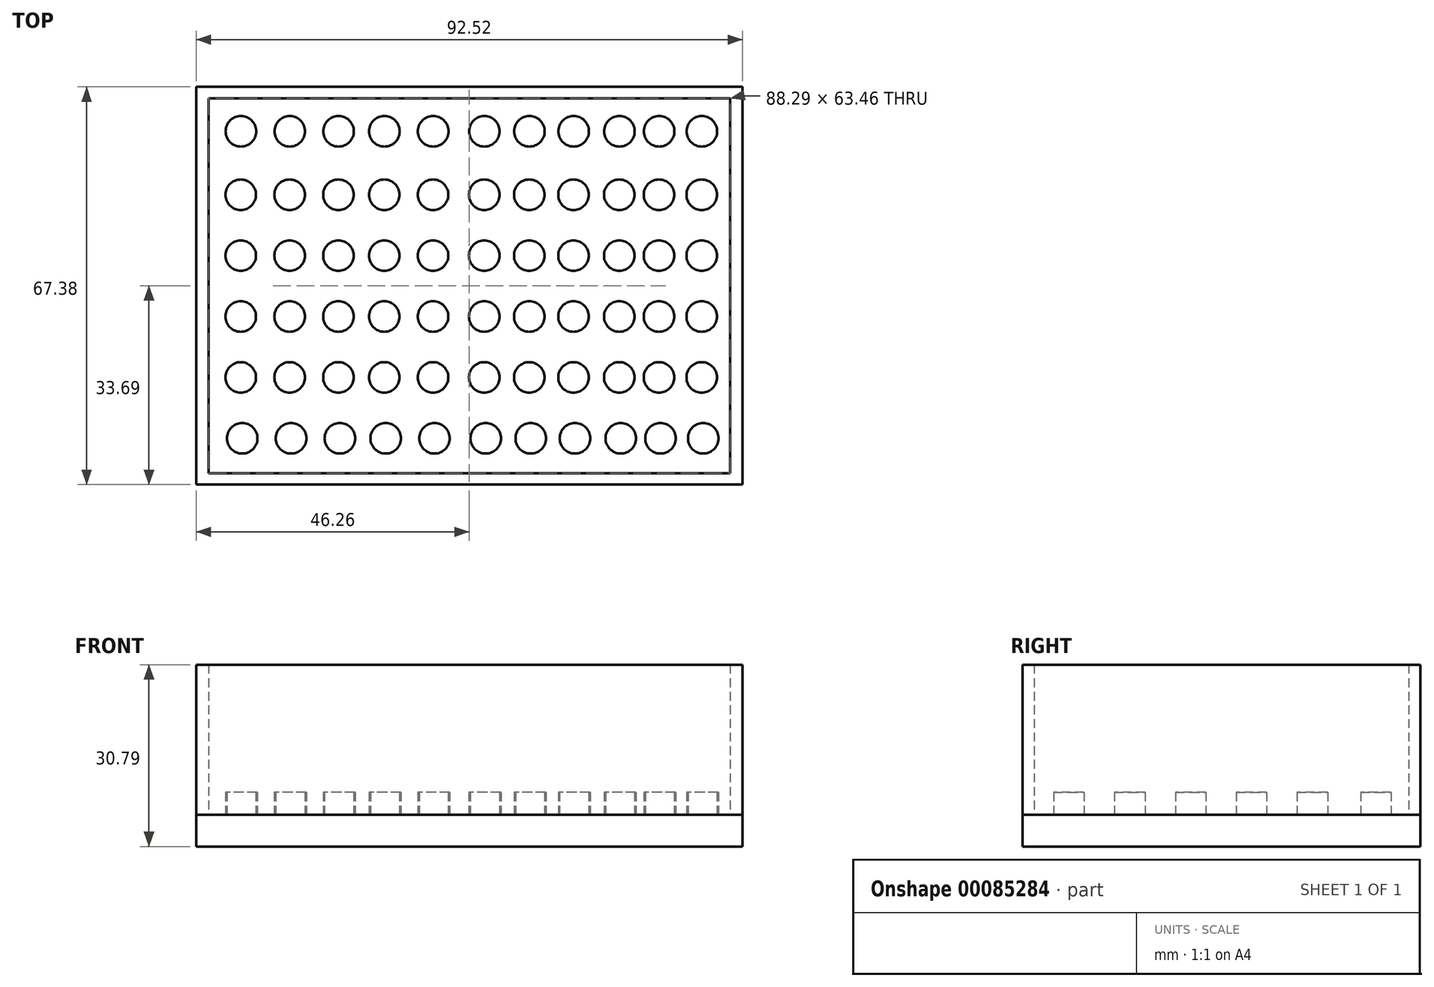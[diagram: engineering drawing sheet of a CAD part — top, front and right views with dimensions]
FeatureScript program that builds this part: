
annotation { "Feature Type Name" : "Feature", "Feature Type Description" : "" }
export const myFeature = defineFeature(function(context is Context, id is Id, definition is map)
    precondition{}
    {
        {
            var Q0;
            Q0=qCreatedBy(makeId("Top.planeOp"),FACE);
            var sketch = newSketch(context, id + "F0", { "sketchPlane" : qUnion([Q0])});
            skLineSegment(sketch, "E0.bottom", {"start": v(47.14, 35.2) * mm, "end": v(-47.14, 35.2) * mm});
            skLineSegment(sketch, "E0.top", {"start": v(47.14, -35.2) * mm, "end": v(-47.14, -35.2) * mm});
            skLineSegment(sketch, "E0.left", {"start": v(47.14, 35.2) * mm, "end": v(47.14, -35.2) * mm});
            skLineSegment(sketch, "E0.right", {"start": v(-47.14, 35.2) * mm, "end": v(-47.14, -35.2) * mm});
            skPoint(sketch, "E0.middle", {"position": v(0, 0) * mm});
            skLineSegment(sketch, "E1.bottom", {"start": v(43.78, 31.59) * mm, "end": v(-43.78, 31.59) * mm});
            skLineSegment(sketch, "E1.top", {"start": v(43.78, -31.59) * mm, "end": v(-43.78, -31.59) * mm});
            skLineSegment(sketch, "E1.left", {"start": v(43.78, 31.59) * mm, "end": v(43.78, -31.59) * mm});
            skLineSegment(sketch, "E1.right", {"start": v(-43.78, 31.59) * mm, "end": v(-43.78, -31.59) * mm});
            skCircle(sketch, "E2", {"center": v(-38.7, 26.16) * mm, "radius": 2.59 * mm});
            skCircle(sketch, "E3", {"center": v(-14.4, 26.16) * mm, "radius": 2.59 * mm});
            skCircle(sketch, "E4", {"center": v(-22.15, 26.16) * mm, "radius": 2.59 * mm});
            skCircle(sketch, "E5", {"center": v(17.67, 26.16) * mm, "radius": 2.59 * mm});
            skCircle(sketch, "E6", {"center": v(39.38, 26.16) * mm, "radius": 2.59 * mm});
            skCircle(sketch, "E7", {"center": v(10.17, 26.16) * mm, "radius": 2.59 * mm});
            skCircle(sketch, "E8", {"center": v(25.42, 26.16) * mm, "radius": 2.59 * mm});
            skCircle(sketch, "E9", {"center": v(-6.12, 26.16) * mm, "radius": 2.59 * mm});
            skCircle(sketch, "E10", {"center": v(32.15, 26.16) * mm, "radius": 2.59 * mm});
            skCircle(sketch, "E11", {"center": v(2.54, 26.16) * mm, "radius": 2.59 * mm});
            skCircle(sketch, "E12", {"center": v(-30.42, 26.16) * mm, "radius": 2.59 * mm});
            skLineSegment(sketch, "E13", {"start": v(-38.7, 26.16) * mm, "end": v(43.78, 26.16) * mm, "construction": true});
            skLineSegment(sketch, "E14", {"start": v(43.78, 26.16) * mm, "end": v(43.78, 20.73) * mm, "construction": true});
            skLineSegment(sketch, "E15", {"start": v(43.78, 20.73) * mm, "end": v(-43.78, 20.73) * mm, "construction": true});
            skLineSegment(sketch, "E16", {"start": v(-43.78, 20.73) * mm, "end": v(-43.78, 15.56) * mm, "construction": true});
            skLineSegment(sketch, "E17", {"start": v(-43.78, 15.56) * mm, "end": v(43.78, 15.56) * mm, "construction": true});
            skLineSegment(sketch, "E18", {"start": v(43.78, 15.56) * mm, "end": v(43.78, 10.39) * mm, "construction": true});
            skLineSegment(sketch, "E19", {"start": v(43.78, 10.39) * mm, "end": v(-43.78, 10.39) * mm, "construction": true});
            skLineSegment(sketch, "E20", {"start": v(-43.78, 10.39) * mm, "end": v(-43.78, 5.22) * mm, "construction": true});
            skLineSegment(sketch, "E21", {"start": v(-43.78, 5.22) * mm, "end": v(43.78, 5.22) * mm, "construction": true});
            skLineSegment(sketch, "E22", {"start": v(43.78, 5.22) * mm, "end": v(43.78, 0) * mm, "construction": true});
            skLineSegment(sketch, "E23", {"start": v(43.78, 0) * mm, "end": v(-43.78, 0) * mm, "construction": true});
            skLineSegment(sketch, "E24", {"start": v(-43.78, 0) * mm, "end": v(-43.78, -5.12) * mm, "construction": true});
            skLineSegment(sketch, "E25", {"start": v(-43.78, -5.12) * mm, "end": v(43.78, -5.12) * mm, "construction": true});
            skLineSegment(sketch, "E26", {"start": v(43.78, -5.12) * mm, "end": v(43.78, -10.3) * mm, "construction": true});
            skLineSegment(sketch, "E27", {"start": v(43.78, -10.3) * mm, "end": v(-43.78, -10.3) * mm, "construction": true});
            skLineSegment(sketch, "E28", {"start": v(-43.78, -10.3) * mm, "end": v(-43.78, -15.47) * mm, "construction": true});
            skLineSegment(sketch, "E29", {"start": v(-43.78, -15.47) * mm, "end": v(43.78, -15.47) * mm, "construction": true});
            skLineSegment(sketch, "E30", {"start": v(43.78, -15.47) * mm, "end": v(43.78, -20.64) * mm, "construction": true});
            skLineSegment(sketch, "E31", {"start": v(43.78, -20.64) * mm, "end": v(-43.78, -20.64) * mm, "construction": true});
            skLineSegment(sketch, "E32", {"start": v(-43.78, -20.64) * mm, "end": v(-43.78, -25.8) * mm, "construction": true});
            skLineSegment(sketch, "E33", {"start": v(-43.78, -25.8) * mm, "end": v(43.78, -25.8) * mm, "construction": true});
            skLineSegment(sketch, "E34", {"start": v(43.78, -25.8) * mm, "end": v(43.78, -31.59) * mm, "construction": true});
            skCircle(sketch, "E35", {"center": v(-38.72, 15.42) * mm, "radius": 2.59 * mm});
            skCircle(sketch, "E36", {"center": v(-14.41, 15.42) * mm, "radius": 2.59 * mm});
            skCircle(sketch, "E37", {"center": v(-22.17, 15.42) * mm, "radius": 2.59 * mm});
            skCircle(sketch, "E38", {"center": v(17.64, 15.42) * mm, "radius": 2.59 * mm});
            skCircle(sketch, "E39", {"center": v(39.36, 15.42) * mm, "radius": 2.59 * mm});
            skCircle(sketch, "E40", {"center": v(10.15, 15.42) * mm, "radius": 2.59 * mm});
            skCircle(sketch, "E41", {"center": v(25.4, 15.42) * mm, "radius": 2.59 * mm});
            skCircle(sketch, "E42", {"center": v(-6.15, 15.42) * mm, "radius": 2.59 * mm});
            skCircle(sketch, "E43", {"center": v(32.12, 15.42) * mm, "radius": 2.59 * mm});
            skCircle(sketch, "E44", {"center": v(2.52, 15.42) * mm, "radius": 2.59 * mm});
            skCircle(sketch, "E45", {"center": v(-30.44, 15.42) * mm, "radius": 2.59 * mm});
            skLineSegment(sketch, "E46", {"start": v(43.75, 15.42) * mm, "end": v(43.75, 9.99) * mm, "construction": true});
            skCircle(sketch, "E47", {"center": v(-38.72, 5.1) * mm, "radius": 2.59 * mm});
            skCircle(sketch, "E48", {"center": v(-14.41, 5.1) * mm, "radius": 2.59 * mm});
            skCircle(sketch, "E49", {"center": v(-22.17, 5.1) * mm, "radius": 2.59 * mm});
            skCircle(sketch, "E50", {"center": v(17.64, 5.1) * mm, "radius": 2.59 * mm});
            skCircle(sketch, "E51", {"center": v(39.36, 5.1) * mm, "radius": 2.59 * mm});
            skCircle(sketch, "E52", {"center": v(10.15, 5.1) * mm, "radius": 2.59 * mm});
            skCircle(sketch, "E53", {"center": v(25.4, 5.1) * mm, "radius": 2.59 * mm});
            skCircle(sketch, "E54", {"center": v(-6.15, 5.1) * mm, "radius": 2.59 * mm});
            skCircle(sketch, "E55", {"center": v(32.12, 5.1) * mm, "radius": 2.59 * mm});
            skCircle(sketch, "E56", {"center": v(2.52, 5.1) * mm, "radius": 2.59 * mm});
            skCircle(sketch, "E57", {"center": v(-30.44, 5.1) * mm, "radius": 2.59 * mm});
            skLineSegment(sketch, "E58", {"start": v(43.75, 5.1) * mm, "end": v(43.75, -0.33) * mm, "construction": true});
            skCircle(sketch, "E59", {"center": v(-38.72, -5.21) * mm, "radius": 2.59 * mm});
            skCircle(sketch, "E60", {"center": v(-14.41, -5.21) * mm, "radius": 2.59 * mm});
            skCircle(sketch, "E61", {"center": v(-22.17, -5.21) * mm, "radius": 2.59 * mm});
            skCircle(sketch, "E62", {"center": v(17.64, -5.21) * mm, "radius": 2.59 * mm});
            skCircle(sketch, "E63", {"center": v(39.36, -5.21) * mm, "radius": 2.59 * mm});
            skCircle(sketch, "E64", {"center": v(10.15, -5.21) * mm, "radius": 2.59 * mm});
            skCircle(sketch, "E65", {"center": v(25.4, -5.21) * mm, "radius": 2.59 * mm});
            skCircle(sketch, "E66", {"center": v(-6.15, -5.21) * mm, "radius": 2.59 * mm});
            skCircle(sketch, "E67", {"center": v(32.12, -5.21) * mm, "radius": 2.59 * mm});
            skCircle(sketch, "E68", {"center": v(2.52, -5.21) * mm, "radius": 2.59 * mm});
            skCircle(sketch, "E69", {"center": v(-30.44, -5.21) * mm, "radius": 2.59 * mm});
            skLineSegment(sketch, "E70", {"start": v(43.75, -5.21) * mm, "end": v(43.75, -10.64) * mm, "construction": true});
            skCircle(sketch, "E71", {"center": v(-38.72, -15.52) * mm, "radius": 2.59 * mm});
            skCircle(sketch, "E72", {"center": v(-14.41, -15.52) * mm, "radius": 2.59 * mm});
            skCircle(sketch, "E73", {"center": v(-22.17, -15.52) * mm, "radius": 2.59 * mm});
            skCircle(sketch, "E74", {"center": v(17.64, -15.52) * mm, "radius": 2.59 * mm});
            skCircle(sketch, "E75", {"center": v(39.36, -15.52) * mm, "radius": 2.59 * mm});
            skCircle(sketch, "E76", {"center": v(10.15, -15.52) * mm, "radius": 2.59 * mm});
            skCircle(sketch, "E77", {"center": v(25.4, -15.52) * mm, "radius": 2.59 * mm});
            skCircle(sketch, "E78", {"center": v(-6.15, -15.52) * mm, "radius": 2.59 * mm});
            skCircle(sketch, "E79", {"center": v(32.12, -15.52) * mm, "radius": 2.59 * mm});
            skCircle(sketch, "E80", {"center": v(2.52, -15.52) * mm, "radius": 2.59 * mm});
            skCircle(sketch, "E81", {"center": v(-30.44, -15.52) * mm, "radius": 2.59 * mm});
            skLineSegment(sketch, "E82", {"start": v(43.75, -15.52) * mm, "end": v(43.75, -20.95) * mm, "construction": true});
            skCircle(sketch, "E83", {"center": v(-38.47, -25.84) * mm, "radius": 2.59 * mm});
            skCircle(sketch, "E84", {"center": v(-14.16, -25.84) * mm, "radius": 2.59 * mm});
            skCircle(sketch, "E85", {"center": v(-21.92, -25.84) * mm, "radius": 2.59 * mm});
            skCircle(sketch, "E86", {"center": v(17.9, -25.84) * mm, "radius": 2.59 * mm});
            skCircle(sketch, "E87", {"center": v(39.6, -25.84) * mm, "radius": 2.59 * mm});
            skCircle(sketch, "E88", {"center": v(10.4, -25.84) * mm, "radius": 2.59 * mm});
            skCircle(sketch, "E89", {"center": v(25.65, -25.84) * mm, "radius": 2.59 * mm});
            skCircle(sketch, "E90", {"center": v(-5.9, -25.84) * mm, "radius": 2.59 * mm});
            skCircle(sketch, "E91", {"center": v(32.37, -25.84) * mm, "radius": 2.59 * mm});
            skCircle(sketch, "E92", {"center": v(2.77, -25.84) * mm, "radius": 2.59 * mm});
            skCircle(sketch, "E93", {"center": v(-30.2, -25.84) * mm, "radius": 2.59 * mm});
            skLineSegment(sketch, "E94", {"start": v(44, -25.84) * mm, "end": v(44, -31.27) * mm, "construction": true});
            skSolve(sketch);
        }
        {
            var Q0;
            Q0=makeQuery(id+"F0.imprint","IMPRINT",FACE,{"disambiguationData":[TD([[makeQuery(id+"F0.imprint","IMPRINT",EDGE,{"derivedFrom":sQuery(id+"F0.wireOp",EDGE,"E42")}),1.0]])]});
            var Q1;
            Q1=makeQuery(id+"F0.imprint","IMPRINT",FACE,{"disambiguationData":[TD([[makeQuery(id+"F0.imprint","IMPRINT",EDGE,{"derivedFrom":sQuery(id+"F0.wireOp",EDGE,"E2")}),1.0]])]});
            var Q2;
            Q2=makeQuery(id+"F0.imprint","IMPRINT",FACE,{"disambiguationData":[TD([[makeQuery(id+"F0.imprint","IMPRINT",EDGE,{"derivedFrom":sQuery(id+"F0.wireOp",EDGE,"E4")}),1.0]])]});
            var Q3;
            Q3=makeQuery(id+"F0.imprint","IMPRINT",FACE,{"disambiguationData":[TD([[makeQuery(id+"F0.imprint","IMPRINT",EDGE,{"derivedFrom":sQuery(id+"F0.wireOp",EDGE,"E76")}),1.0]])]});
            var Q4;
            Q4=makeQuery(id+"F0.imprint","IMPRINT",FACE,{"disambiguationData":[TD([[makeQuery(id+"F0.imprint","IMPRINT",EDGE,{"derivedFrom":sQuery(id+"F0.wireOp",EDGE,"E93")}),1.0]])]});
            var Q5;
            Q5=makeQuery(id+"F0.imprint","IMPRINT",FACE,{"disambiguationData":[TD([[makeQuery(id+"F0.imprint","IMPRINT",EDGE,{"derivedFrom":sQuery(id+"F0.wireOp",EDGE,"E73")}),1.0]])]});
            var Q6;
            Q6=makeQuery(id+"F0.imprint","IMPRINT",FACE,{"disambiguationData":[TD([[makeQuery(id+"F0.imprint","IMPRINT",EDGE,{"derivedFrom":sQuery(id+"F0.wireOp",EDGE,"E8")}),1.0]])]});
            var Q7;
            Q7=makeQuery(id+"F0.imprint","IMPRINT",FACE,{"disambiguationData":[TD([[makeQuery(id+"F0.imprint","IMPRINT",EDGE,{"derivedFrom":sQuery(id+"F0.wireOp",EDGE,"E41")}),1.0]])]});
            var Q8;
            Q8=makeQuery(id+"F0.imprint","IMPRINT",FACE,{"disambiguationData":[TD([[makeQuery(id+"F0.imprint","IMPRINT",EDGE,{"derivedFrom":sQuery(id+"F0.wireOp",EDGE,"E64")}),1.0]])]});
            var Q9;
            Q9=makeQuery(id+"F0.imprint","IMPRINT",FACE,{"disambiguationData":[TD([[makeQuery(id+"F0.imprint","IMPRINT",EDGE,{"derivedFrom":sQuery(id+"F0.wireOp",EDGE,"E12")}),1.0]])]});
            var Q10;
            Q10=makeQuery(id+"F0.imprint","IMPRINT",FACE,{"disambiguationData":[TD([[makeQuery(id+"F0.imprint","IMPRINT",EDGE,{"derivedFrom":sQuery(id+"F0.wireOp",EDGE,"E74")}),1.0]])]});
            var Q11;
            Q11=makeQuery(id+"F0.imprint","IMPRINT",FACE,{"disambiguationData":[TD([[makeQuery(id+"F0.imprint","IMPRINT",EDGE,{"derivedFrom":sQuery(id+"F0.wireOp",EDGE,"E65")}),1.0]])]});
            var Q12;
            Q12=makeQuery(id+"F0.imprint","IMPRINT",FACE,{"disambiguationData":[TD([[makeQuery(id+"F0.imprint","IMPRINT",EDGE,{"derivedFrom":sQuery(id+"F0.wireOp",EDGE,"E40")}),1.0]])]});
            var Q13;
            Q13=makeQuery(id+"F0.imprint","IMPRINT",FACE,{"disambiguationData":[TD([[makeQuery(id+"F0.imprint","IMPRINT",EDGE,{"derivedFrom":sQuery(id+"F0.wireOp",EDGE,"E37")}),1.0]])]});
            var Q14;
            Q14=makeQuery(id+"F0.imprint","IMPRINT",FACE,{"disambiguationData":[TD([[makeQuery(id+"F0.imprint","IMPRINT",EDGE,{"derivedFrom":sQuery(id+"F0.wireOp",EDGE,"E36")}),1.0]])]});
            var Q15;
            Q15=makeQuery(id+"F0.imprint","IMPRINT",FACE,{"disambiguationData":[TD([[makeQuery(id+"F0.imprint","IMPRINT",EDGE,{"derivedFrom":sQuery(id+"F0.wireOp",EDGE,"E38")}),1.0]])]});
            var Q16;
            Q16=makeQuery(id+"F0.imprint","IMPRINT",FACE,{"disambiguationData":[TD([[makeQuery(id+"F0.imprint","IMPRINT",EDGE,{"derivedFrom":sQuery(id+"F0.wireOp",EDGE,"E62")}),1.0]])]});
            var Q17;
            Q17=makeQuery(id+"F0.imprint","IMPRINT",FACE,{"disambiguationData":[TD([[makeQuery(id+"F0.imprint","IMPRINT",EDGE,{"derivedFrom":sQuery(id+"F0.wireOp",EDGE,"E61")}),1.0]])]});
            var Q18;
            Q18=makeQuery(id+"F0.imprint","IMPRINT",FACE,{"disambiguationData":[TD([[makeQuery(id+"F0.imprint","IMPRINT",EDGE,{"derivedFrom":sQuery(id+"F0.wireOp",EDGE,"E43")}),1.0]])]});
            var Q19;
            Q19=makeQuery(id+"F0.imprint","IMPRINT",FACE,{"disambiguationData":[TD([[makeQuery(id+"F0.imprint","IMPRINT",EDGE,{"derivedFrom":sQuery(id+"F0.wireOp",EDGE,"E85")}),1.0]])]});
            var Q20;
            Q20=makeQuery(id+"F0.imprint","IMPRINT",FACE,{"disambiguationData":[TD([[makeQuery(id+"F0.imprint","IMPRINT",EDGE,{"derivedFrom":sQuery(id+"F0.wireOp",EDGE,"E77")}),1.0]])]});
            var Q21;
            Q21=makeQuery(id+"F0.imprint","IMPRINT",FACE,{"disambiguationData":[TD([[makeQuery(id+"F0.imprint","IMPRINT",EDGE,{"derivedFrom":sQuery(id+"F0.wireOp",EDGE,"E59")}),1.0]])]});
            var Q22;
            Q22=makeQuery(id+"F0.imprint","IMPRINT",FACE,{"disambiguationData":[TD([[makeQuery(id+"F0.imprint","IMPRINT",EDGE,{"derivedFrom":sQuery(id+"F0.wireOp",EDGE,"E57")}),1.0]])]});
            var Q23;
            Q23=makeQuery(id+"F0.imprint","IMPRINT",FACE,{"disambiguationData":[TD([[makeQuery(id+"F0.imprint","IMPRINT",EDGE,{"derivedFrom":sQuery(id+"F0.wireOp",EDGE,"E75")}),1.0]])]});
            var Q24;
            Q24=makeQuery(id+"F0.imprint","IMPRINT",FACE,{"disambiguationData":[TD([[makeQuery(id+"F0.imprint","IMPRINT",EDGE,{"derivedFrom":sQuery(id+"F0.wireOp",EDGE,"E6")}),1.0]])]});
            var Q25;
            Q25=makeQuery(id+"F0.imprint","IMPRINT",FACE,{"disambiguationData":[TD([[makeQuery(id+"F0.imprint","IMPRINT",EDGE,{"derivedFrom":sQuery(id+"F0.wireOp",EDGE,"E81")}),1.0]])]});
            var Q26;
            Q26=makeQuery(id+"F0.imprint","IMPRINT",FACE,{"disambiguationData":[TD([[makeQuery(id+"F0.imprint","IMPRINT",EDGE,{"derivedFrom":sQuery(id+"F0.wireOp",EDGE,"E5")}),1.0]])]});
            var Q27;
            Q27=makeQuery(id+"F0.imprint","IMPRINT",FACE,{"disambiguationData":[TD([[makeQuery(id+"F0.imprint","IMPRINT",EDGE,{"derivedFrom":sQuery(id+"F0.wireOp",EDGE,"E3")}),1.0]])]});
            var Q28;
            Q28=makeQuery(id+"F0.imprint","IMPRINT",FACE,{"disambiguationData":[TD([[makeQuery(id+"F0.imprint","IMPRINT",EDGE,{"derivedFrom":sQuery(id+"F0.wireOp",EDGE,"E92")}),1.0]])]});
            var Q29;
            Q29=makeQuery(id+"F0.imprint","IMPRINT",FACE,{"disambiguationData":[TD([[makeQuery(id+"F0.imprint","IMPRINT",EDGE,{"derivedFrom":sQuery(id+"F0.wireOp",EDGE,"E90")}),1.0]])]});
            var Q30;
            Q30=makeQuery(id+"F0.imprint","IMPRINT",FACE,{"disambiguationData":[TD([[makeQuery(id+"F0.imprint","IMPRINT",EDGE,{"derivedFrom":sQuery(id+"F0.wireOp",EDGE,"E44")}),1.0]])]});
            var Q31;
            Q31=makeQuery(id+"F0.imprint","IMPRINT",FACE,{"disambiguationData":[TD([[makeQuery(id+"F0.imprint","IMPRINT",EDGE,{"derivedFrom":sQuery(id+"F0.wireOp",EDGE,"E66")}),1.0]])]});
            var Q32;
            Q32=makeQuery(id+"F0.imprint","IMPRINT",FACE,{"disambiguationData":[TD([[makeQuery(id+"F0.imprint","IMPRINT",EDGE,{"derivedFrom":sQuery(id+"F0.wireOp",EDGE,"E55")}),1.0]])]});
            var Q33;
            Q33=makeQuery(id+"F0.imprint","IMPRINT",FACE,{"disambiguationData":[TD([[makeQuery(id+"F0.imprint","IMPRINT",EDGE,{"derivedFrom":sQuery(id+"F0.wireOp",EDGE,"E49")}),1.0]])]});
            var Q34;
            Q34=makeQuery(id+"F0.imprint","IMPRINT",FACE,{"disambiguationData":[TD([[makeQuery(id+"F0.imprint","IMPRINT",EDGE,{"derivedFrom":sQuery(id+"F0.wireOp",EDGE,"E35")}),1.0]])]});
            var Q35;
            Q35=makeQuery(id+"F0.imprint","IMPRINT",FACE,{"disambiguationData":[TD([[makeQuery(id+"F0.imprint","IMPRINT",EDGE,{"derivedFrom":sQuery(id+"F0.wireOp",EDGE,"E84")}),1.0]])]});
            var Q36;
            Q36=makeQuery(id+"F0.imprint","IMPRINT",FACE,{"disambiguationData":[TD([[makeQuery(id+"F0.imprint","IMPRINT",EDGE,{"derivedFrom":sQuery(id+"F0.wireOp",EDGE,"E11")}),1.0]])]});
            var Q37;
            Q37=makeQuery(id+"F0.imprint","IMPRINT",FACE,{"disambiguationData":[TD([[makeQuery(id+"F0.imprint","IMPRINT",EDGE,{"derivedFrom":sQuery(id+"F0.wireOp",EDGE,"E9")}),1.0]])]});
            var Q38;
            Q38=makeQuery(id+"F0.imprint","IMPRINT",FACE,{"disambiguationData":[TD([[makeQuery(id+"F0.imprint","IMPRINT",EDGE,{"derivedFrom":sQuery(id+"F0.wireOp",EDGE,"E10")}),1.0]])]});
            var Q39;
            Q39=makeQuery(id+"F0.imprint","IMPRINT",FACE,{"disambiguationData":[TD([[makeQuery(id+"F0.imprint","IMPRINT",EDGE,{"derivedFrom":sQuery(id+"F0.wireOp",EDGE,"E7")}),1.0]])]});
            var Q40;
            Q40=makeQuery(id+"F0.imprint","IMPRINT",FACE,{"disambiguationData":[TD([[makeQuery(id+"F0.imprint","IMPRINT",EDGE,{"derivedFrom":sQuery(id+"F0.wireOp",EDGE,"E47")}),1.0]])]});
            var Q41;
            Q41=makeQuery(id+"F0.imprint","IMPRINT",FACE,{"disambiguationData":[TD([[makeQuery(id+"F0.imprint","IMPRINT",EDGE,{"derivedFrom":sQuery(id+"F0.wireOp",EDGE,"E51")}),1.0]])]});
            var Q42;
            Q42=makeQuery(id+"F0.imprint","IMPRINT",FACE,{"disambiguationData":[TD([[makeQuery(id+"F0.imprint","IMPRINT",EDGE,{"derivedFrom":sQuery(id+"F0.wireOp",EDGE,"E68")}),1.0]])]});
            var Q43;
            Q43=makeQuery(id+"F0.imprint","IMPRINT",FACE,{"disambiguationData":[TD([[makeQuery(id+"F0.imprint","IMPRINT",EDGE,{"derivedFrom":sQuery(id+"F0.wireOp",EDGE,"E86")}),1.0]])]});
            var Q44;
            Q44=makeQuery(id+"F0.imprint","IMPRINT",FACE,{"disambiguationData":[TD([[makeQuery(id+"F0.imprint","IMPRINT",EDGE,{"derivedFrom":sQuery(id+"F0.wireOp",EDGE,"E48")}),1.0]])]});
            var Q45;
            Q45=makeQuery(id+"F0.imprint","IMPRINT",FACE,{"disambiguationData":[TD([[makeQuery(id+"F0.imprint","IMPRINT",EDGE,{"derivedFrom":sQuery(id+"F0.wireOp",EDGE,"E83")}),1.0]])]});
            var Q46;
            Q46=makeQuery(id+"F0.imprint","IMPRINT",FACE,{"disambiguationData":[TD([[makeQuery(id+"F0.imprint","IMPRINT",EDGE,{"derivedFrom":sQuery(id+"F0.wireOp",EDGE,"E56")}),1.0]])]});
            var Q47;
            Q47=makeQuery(id+"F0.imprint","IMPRINT",FACE,{"disambiguationData":[TD([[makeQuery(id+"F0.imprint","IMPRINT",EDGE,{"derivedFrom":sQuery(id+"F0.wireOp",EDGE,"E91")}),1.0]])]});
            var Q48;
            Q48=makeQuery(id+"F0.imprint","IMPRINT",FACE,{"disambiguationData":[TD([[makeQuery(id+"F0.imprint","IMPRINT",EDGE,{"derivedFrom":sQuery(id+"F0.wireOp",EDGE,"E39")}),1.0]])]});
            var Q49;
            Q49=makeQuery(id+"F0.imprint","IMPRINT",FACE,{"disambiguationData":[TD([[makeQuery(id+"F0.imprint","IMPRINT",EDGE,{"derivedFrom":sQuery(id+"F0.wireOp",EDGE,"E63")}),1.0]])]});
            var Q50;
            Q50=makeQuery(id+"F0.imprint","IMPRINT",FACE,{"disambiguationData":[TD([[makeQuery(id+"F0.imprint","IMPRINT",EDGE,{"derivedFrom":sQuery(id+"F0.wireOp",EDGE,"E45")}),1.0]])]});
            var Q51;
            Q51=makeQuery(id+"F0.imprint","IMPRINT",FACE,{"disambiguationData":[TD([[makeQuery(id+"F0.imprint","IMPRINT",EDGE,{"derivedFrom":sQuery(id+"F0.wireOp",EDGE,"E80")}),1.0]])]});
            var Q52;
            Q52=makeQuery(id+"F0.imprint","IMPRINT",FACE,{"disambiguationData":[TD([[makeQuery(id+"F0.imprint","IMPRINT",EDGE,{"derivedFrom":sQuery(id+"F0.wireOp",EDGE,"E52")}),1.0]])]});
            var Q53;
            Q53=makeQuery(id+"F0.imprint","IMPRINT",FACE,{"disambiguationData":[TD([[makeQuery(id+"F0.imprint","IMPRINT",EDGE,{"derivedFrom":sQuery(id+"F0.wireOp",EDGE,"E69")}),1.0]])]});
            var Q54;
            Q54=makeQuery(id+"F0.imprint","IMPRINT",FACE,{"disambiguationData":[TD([[makeQuery(id+"F0.imprint","IMPRINT",EDGE,{"derivedFrom":sQuery(id+"F0.wireOp",EDGE,"E87")}),1.0]])]});
            var Q55;
            Q55=makeQuery(id+"F0.imprint","IMPRINT",FACE,{"disambiguationData":[TD([[makeQuery(id+"F0.imprint","IMPRINT",EDGE,{"derivedFrom":sQuery(id+"F0.wireOp",EDGE,"E54")}),1.0]])]});
            var Q56;
            Q56=makeQuery(id+"F0.imprint","IMPRINT",FACE,{"disambiguationData":[TD([[makeQuery(id+"F0.imprint","IMPRINT",EDGE,{"derivedFrom":sQuery(id+"F0.wireOp",EDGE,"E79")}),1.0]])]});
            var Q57;
            Q57=makeQuery(id+"F0.imprint","IMPRINT",FACE,{"disambiguationData":[TD([[makeQuery(id+"F0.imprint","IMPRINT",EDGE,{"derivedFrom":sQuery(id+"F0.wireOp",EDGE,"E72")}),1.0]])]});
            var Q58;
            Q58=makeQuery(id+"F0.imprint","IMPRINT",FACE,{"disambiguationData":[TD([[makeQuery(id+"F0.imprint","IMPRINT",EDGE,{"derivedFrom":sQuery(id+"F0.wireOp",EDGE,"E89")}),1.0]])]});
            var Q59;
            Q59=makeQuery(id+"F0.imprint","IMPRINT",FACE,{"disambiguationData":[TD([[makeQuery(id+"F0.imprint","IMPRINT",EDGE,{"derivedFrom":sQuery(id+"F0.wireOp",EDGE,"E53")}),1.0]])]});
            var Q60;
            Q60=makeQuery(id+"F0.imprint","IMPRINT",FACE,{"disambiguationData":[TD([[makeQuery(id+"F0.imprint","IMPRINT",EDGE,{"derivedFrom":sQuery(id+"F0.wireOp",EDGE,"E71")}),1.0]])]});
            var Q61;
            Q61=makeQuery(id+"F0.imprint","IMPRINT",FACE,{"disambiguationData":[TD([[makeQuery(id+"F0.imprint","IMPRINT",EDGE,{"derivedFrom":sQuery(id+"F0.wireOp",EDGE,"E78")}),1.0]])]});
            var Q62;
            Q62=makeQuery(id+"F0.imprint","IMPRINT",FACE,{"disambiguationData":[TD([[makeQuery(id+"F0.imprint","IMPRINT",EDGE,{"derivedFrom":sQuery(id+"F0.wireOp",EDGE,"E88")}),1.0]])]});
            var Q63;
            Q63=makeQuery(id+"F0.imprint","IMPRINT",FACE,{"disambiguationData":[TD([[makeQuery(id+"F0.imprint","IMPRINT",EDGE,{"derivedFrom":sQuery(id+"F0.wireOp",EDGE,"E50")}),1.0]])]});
            var Q64;
            Q64=makeQuery(id+"F0.imprint","IMPRINT",FACE,{"disambiguationData":[TD([[makeQuery(id+"F0.imprint","IMPRINT",EDGE,{"derivedFrom":sQuery(id+"F0.wireOp",EDGE,"E67")}),1.0]])]});
            var Q65;
            Q65=makeQuery(id+"F0.imprint","IMPRINT",FACE,{"disambiguationData":[TD([[makeQuery(id+"F0.imprint","IMPRINT",EDGE,{"derivedFrom":sQuery(id+"F0.wireOp",EDGE,"E60")}),1.0]])]});
            extrude(context, id + "F1", {"entities" : qUnion([Q0, Q1, Q2, Q3, Q4, Q5, Q6, Q7, Q8, Q9, Q10, Q11, Q12, Q13, Q14, Q15, Q16, Q17, Q18, Q19, Q20, Q21, Q22, Q23, Q24, Q25, Q26, Q27, Q28, Q29, Q30, Q31, Q32, Q33, Q34, Q35, Q36, Q37, Q38, Q39, Q40, Q41, Q42, Q43, Q44, Q45, Q46, Q47, Q48, Q49, Q50, Q51, Q52, Q53, Q54, Q55, Q56, Q57, Q58, Q59, Q60, Q61, Q62, Q63, Q64, Q65]), "depth" : 3.8 * mm});
        }
        {
            var Q0;
            Q0=qCreatedBy(makeId("Top.planeOp"),FACE);
            var sketch = newSketch(context, id + "F2", { "sketchPlane" : qUnion([Q0])});
            skLineSegment(sketch, "E95.bottom", {"start": v(44.14, 31.73) * mm, "end": v(-44.14, 31.73) * mm});
            skLineSegment(sketch, "E95.top", {"start": v(44.14, -31.73) * mm, "end": v(-44.14, -31.73) * mm});
            skLineSegment(sketch, "E95.left", {"start": v(44.14, 31.73) * mm, "end": v(44.14, -31.73) * mm});
            skLineSegment(sketch, "E95.right", {"start": v(-44.14, 31.73) * mm, "end": v(-44.14, -31.73) * mm});
            skPoint(sketch, "E95.middle", {"position": v(0, 0) * mm});
            skLineSegment(sketch, "E96.bottom", {"start": v(46.26, 33.69) * mm, "end": v(-46.26, 33.69) * mm});
            skLineSegment(sketch, "E96.top", {"start": v(46.26, -33.69) * mm, "end": v(-46.26, -33.69) * mm});
            skLineSegment(sketch, "E96.left", {"start": v(46.26, 33.69) * mm, "end": v(46.26, -33.69) * mm});
            skLineSegment(sketch, "E96.right", {"start": v(-46.26, 33.69) * mm, "end": v(-46.26, -33.69) * mm});
            skSolve(sketch);
        }
        {
            var Q0;
            Q0=makeQuery(id+"F2.imprint","IMPRINT",FACE,{"disambiguationData":[TD([[makeQuery(id+"F2.imprint","IMPRINT",EDGE,{"derivedFrom":sQuery(id+"F2.wireOp",EDGE,"E95.bottom")}),-1.0]])]});
            extrude(context, id + "F3", {"entities" : qUnion([Q0]), "depth" : 25.4 * mm});
        }
        {
            var Q0;
            Q0=makeQuery(id+"F3.opExtrude","CAP_FACE",FACE,{"disambiguationData":[OSD([sQuery(id+"F2.wireOp",EDGE,"E95.bottom"),sQuery(id+"F2.wireOp",EDGE,"E95.top"),sQuery(id+"F2.wireOp",EDGE,"E95.left"),sQuery(id+"F2.wireOp",EDGE,"E95.right"),sQuery(id+"F2.wireOp",EDGE,"E96.bottom"),sQuery(id+"F2.wireOp",EDGE,"E96.top"),sQuery(id+"F2.wireOp",EDGE,"E96.left"),sQuery(id+"F2.wireOp",EDGE,"E96.right")])],"isStart":true});
            var sketch = newSketch(context, id + "F4", { "sketchPlane" : qUnion([Q0])});
            skLineSegment(sketch, "E97.bottom", {"start": v(46.26, 33.69) * mm, "end": v(-46.26, 33.69) * mm});
            skLineSegment(sketch, "E97.top", {"start": v(46.26, -33.69) * mm, "end": v(-46.26, -33.69) * mm});
            skLineSegment(sketch, "E97.left", {"start": v(46.26, 33.69) * mm, "end": v(46.26, -33.69) * mm});
            skLineSegment(sketch, "E97.right", {"start": v(-46.26, 33.69) * mm, "end": v(-46.26, -33.69) * mm});
            skPoint(sketch, "E97.middle", {"position": v(0, 0) * mm});
            skSolve(sketch);
        }
        {
            var Q0;
            Q0 = qSketchRegion(id + "F4", true);
            extrude(context, id + "F5", {"entities" : qUnion([Q0]), "depth" : 5.4 * mm});
        }
    });
